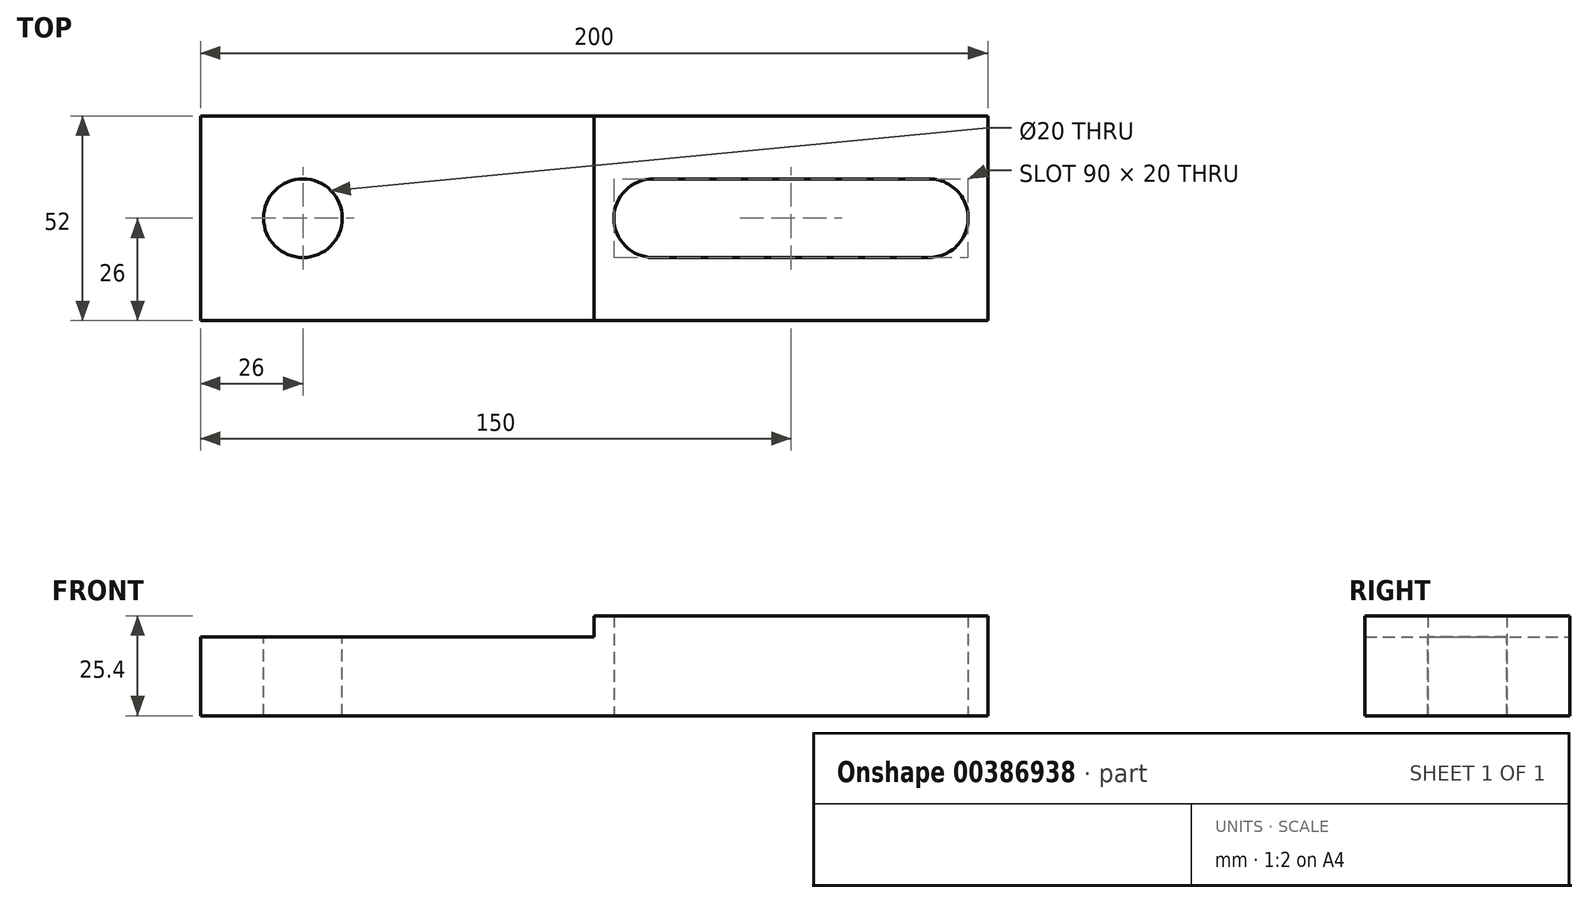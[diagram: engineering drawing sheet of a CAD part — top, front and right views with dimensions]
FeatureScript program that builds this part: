
annotation { "Feature Type Name" : "Feature", "Feature Type Description" : "" }
export const myFeature = defineFeature(function(context is Context, id is Id, definition is map)
    precondition{}
    {
        {
            var Q0;
            Q0=qCreatedBy(makeId("Top.planeOp"),FACE);
            var sketch = newSketch(context, id + "F0", { "sketchPlane" : qUnion([Q0])});
            skLineSegment(sketch, "E0.bottom", {"start": v(0, 0) * mm, "end": v(100, 0) * mm});
            skLineSegment(sketch, "E0.top", {"start": v(0, 52) * mm, "end": v(100, 52) * mm});
            skLineSegment(sketch, "E0.left", {"start": v(0, 0) * mm, "end": v(0, 52) * mm});
            skLineSegment(sketch, "E0.right", {"start": v(100, 0) * mm, "end": v(100, 52) * mm});
            skLineSegment(sketch, "E1", {"start": v(100, 26) * mm, "end": v(85, 26) * mm});
            skCircle(sketch, "E2", {"center": v(85, 26) * mm, "radius": 10 * mm});
            skLineSegment(sketch, "E3", {"start": v(0, 26) * mm, "end": v(15, 26) * mm});
            skPoint(sketch, "E3.endSnap0", {"position": v(0, 26) * mm});
            skCircle(sketch, "E4", {"center": v(15, 26) * mm, "radius": 10 * mm});
            skLineSegment(sketch, "E5", {"start": v(14.98, 36) * mm, "end": v(15, 16) * mm});
            skLineSegment(sketch, "E6", {"start": v(84.99, 36) * mm, "end": v(85, 16) * mm});
            skLineSegment(sketch, "E7", {"start": v(15, 16) * mm, "end": v(85, 16) * mm});
            skLineSegment(sketch, "E8", {"start": v(14.98, 36) * mm, "end": v(84.99, 36) * mm});
            skSolve(sketch);
        }
        {
            var Q0;
            {var subQ3=sQuery(id+"F0.wireOp",EDGE,"E0.bottom");Q0=makeQuery(id+"F0.imprint","IMPRINT",FACE,{"disambiguationData":[TD([[makeQuery(id+"F0.imprint","IMPRINT",EDGE,{"derivedFrom":subQ3}),1.0]])]});}
            extrude(context, id + "F1", {"entities" : qUnion([Q0]), "depth" : 20 * mm});
        }
        {
            var Q0;
            Q0=makeQuery(id+"F1.opExtrude","CAP_FACE",FACE,{"disambiguationData":[OSD([sQuery(id+"F0.wireOp",EDGE,"E0.bottom"),sQuery(id+"F0.wireOp",EDGE,"E0.top"),sQuery(id+"F0.wireOp",EDGE,"E0.left"),sQuery(id+"F0.wireOp",EDGE,"E0.right"),sQuery(id+"F0.wireOp",EDGE,"E2"),sQuery(id+"F0.wireOp",EDGE,"E4")])],"isStart":false});
            var sketch = newSketch(context, id + "F2", { "sketchPlane" : qUnion([Q0])});
            skLineSegment(sketch, "E9", {"start": v(15.68, 35.98) * mm, "end": v(15.68, 16.02) * mm});
            skLineSegment(sketch, "E10", {"start": v(85.68, 35.98) * mm, "end": v(85.68, 16.02) * mm});
            skLineSegment(sketch, "E11", {"start": v(15.68, 16.02) * mm, "end": v(85.68, 16.02) * mm});
            skLineSegment(sketch, "E12", {"start": v(15.68, 35.98) * mm, "end": v(85.68, 35.98) * mm});
            skSolve(sketch);
        }
        {
            var Q0;
            Q0 = qSketchRegion(id + "F2", true);
            extrude(context, id + "F3", {"entities" : qUnion([Q0]), "operationType" : NewBodyOperationType.REMOVE, "oppositeDirection" : true, "depth" : 25.4 * mm});
        }
        {
            var Q0;
            Q0 = qSketchRegion(id + "F2", true);
            extrude(context, id + "F4", {"entities" : qUnion([Q0]), "operationType" : NewBodyOperationType.REMOVE, "oppositeDirection" : true, "depth" : 25.4 * mm});
        }
        {
            var Q0;
            Q0=qCreatedBy(makeId("Top.planeOp"),FACE);
            var sketch = newSketch(context, id + "F5", { "sketchPlane" : qUnion([Q0])});
            skLineSegment(sketch, "E13.bottom", {"start": v(0, 0) * mm, "end": v(-100, 0) * mm});
            skLineSegment(sketch, "E13.top", {"start": v(0, 52) * mm, "end": v(-100, 52) * mm});
            skLineSegment(sketch, "E13.left", {"start": v(0, 0) * mm, "end": v(0, 52) * mm});
            skLineSegment(sketch, "E13.right", {"start": v(-100, 0) * mm, "end": v(-100, 52) * mm});
            skSolve(sketch);
        }
        {
            var Q0;
            Q0 = qSketchRegion(id + "F5", true);
            extrude(context, id + "F6", {"entities" : qUnion([Q0]), "operationType" : NewBodyOperationType.ADD, "depth" : 20 * mm});
        }
        {
            var Q0;
            Q0=makeQuery(id+"F6.boolean.opBoolean","MERGE",FACE,{"derivedFrom":[makeQuery(id+"F1.opExtrude","CAP_FACE",FACE,{"disambiguationData":[OSD([sQuery(id+"F0.wireOp",EDGE,"E0.bottom"),sQuery(id+"F0.wireOp",EDGE,"E0.top"),sQuery(id+"F0.wireOp",EDGE,"E0.left"),sQuery(id+"F0.wireOp",EDGE,"E0.right"),sQuery(id+"F0.wireOp",EDGE,"E2"),sQuery(id+"F0.wireOp",EDGE,"E4")])],"isStart":false}),makeQuery(id+"F6.opExtrude","CAP_FACE",FACE,{"disambiguationData":[OSD([sQuery(id+"F5.wireOp",EDGE,"E13.bottom"),sQuery(id+"F5.wireOp",EDGE,"E13.top"),sQuery(id+"F5.wireOp",EDGE,"E13.left"),sQuery(id+"F5.wireOp",EDGE,"E13.right")])],"isStart":false})]});
            var sketch = newSketch(context, id + "F7", { "sketchPlane" : qUnion([Q0])});
            skLineSegment(sketch, "E14", {"start": v(-100, 26) * mm, "end": v(-74, 26) * mm});
            skCircle(sketch, "E15", {"center": v(-74, 26) * mm, "radius": 10 * mm});
            skSolve(sketch);
        }
        {
            var Q0;
            Q0 = qSketchRegion(id + "F7", true);
            extrude(context, id + "F8", {"entities" : qUnion([Q0]), "operationType" : NewBodyOperationType.REMOVE, "oppositeDirection" : true, "depth" : 25.4 * mm});
        }
        {
            var Q0;
            Q0 = qSketchRegion(id + "F0", true);
            extrude(context, id + "F9", {"entities" : qUnion([Q0]), "operationType" : NewBodyOperationType.ADD, "depth" : 25.4 * mm});
        }
    });
